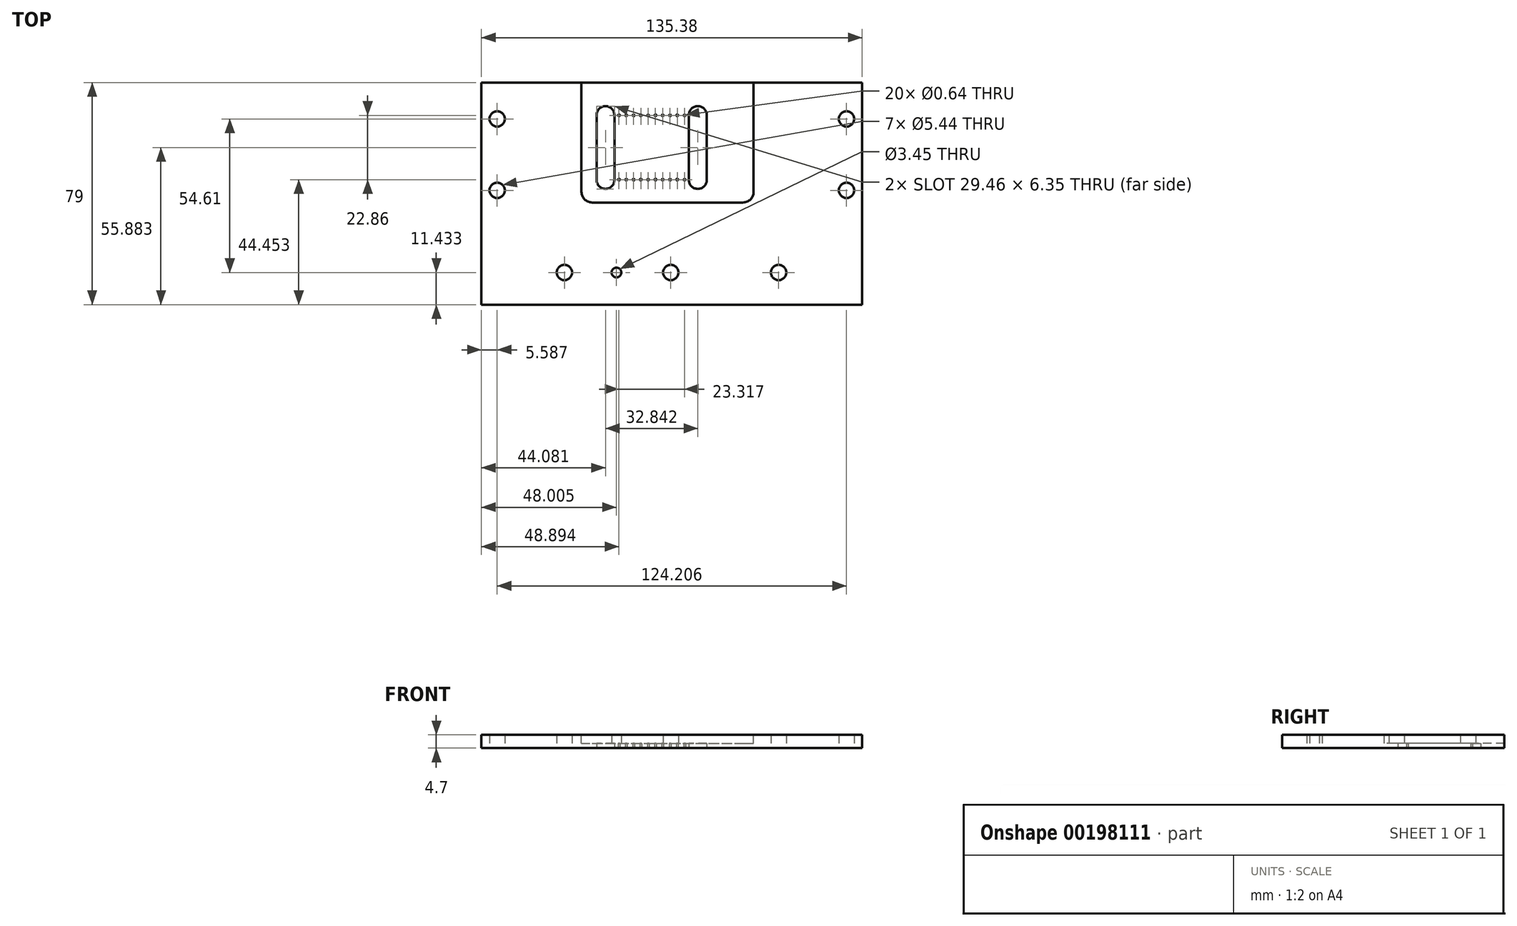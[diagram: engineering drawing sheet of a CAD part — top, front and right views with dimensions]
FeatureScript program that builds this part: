
annotation { "Feature Type Name" : "Feature", "Feature Type Description" : "" }
export const myFeature = defineFeature(function(context is Context, id is Id, definition is map)
    precondition{}
    {
        {
            var Q0;
            Q0=qCreatedBy(makeId("Top.planeOp"),FACE);
            var sketch = newSketch(context, id + "F0", { "sketchPlane" : qUnion([Q0])});
            skLineSegment(sketch, "E0.bottom", {"start": v(-67.7, 39.5) * mm, "end": v(67.7, 39.5) * mm});
            skLineSegment(sketch, "E0.top", {"start": v(-67.7, -39.5) * mm, "end": v(67.7, -39.5) * mm});
            skLineSegment(sketch, "E0.left", {"start": v(-67.7, 39.5) * mm, "end": v(-67.7, -39.5) * mm});
            skLineSegment(sketch, "E0.right", {"start": v(67.7, 39.5) * mm, "end": v(67.7, -39.5) * mm});
            skPoint(sketch, "E0.middle", {"position": v(0, 0) * mm});
            skCircle(sketch, "E1", {"center": v(-62.1, 26.54) * mm, "radius": 2.72 * mm});
            skCircle(sketch, "E2", {"center": v(62.1, 26.54) * mm, "radius": 2.72 * mm});
            skCircle(sketch, "E3", {"center": v(-62.1, 1.14) * mm, "radius": 2.72 * mm});
            skCircle(sketch, "E4", {"center": v(62.1, 1.14) * mm, "radius": 2.72 * mm});
            skCircle(sketch, "E5", {"center": v(37.95, -28.07) * mm, "radius": 2.72 * mm});
            skCircle(sketch, "E6", {"center": v(-38.2, -28.07) * mm, "radius": 2.72 * mm});
            skCircle(sketch, "E7", {"center": v(-18.8, 27.81) * mm, "radius": 0.32 * mm});
            skCircle(sketch, "E8.1.0.0", {"center": v(-16.2, 27.81) * mm, "radius": 0.32 * mm});
            skCircle(sketch, "E8.2.0.0", {"center": v(-13.61, 27.81) * mm, "radius": 0.32 * mm});
            skCircle(sketch, "E8.3.0.0", {"center": v(-11.02, 27.81) * mm, "radius": 0.32 * mm});
            skCircle(sketch, "E8.4.0.0", {"center": v(-8.43, 27.81) * mm, "radius": 0.32 * mm});
            skCircle(sketch, "E8.5.0.0", {"center": v(-5.84, 27.81) * mm, "radius": 0.32 * mm});
            skCircle(sketch, "E8.6.0.0", {"center": v(-3.25, 27.81) * mm, "radius": 0.32 * mm});
            skCircle(sketch, "E8.7.0.0", {"center": v(-0.66, 27.81) * mm, "radius": 0.32 * mm});
            skCircle(sketch, "E8.8.0.0", {"center": v(1.93, 27.81) * mm, "radius": 0.32 * mm});
            skCircle(sketch, "E8.9.0.0", {"center": v(4.52, 27.81) * mm, "radius": 0.32 * mm});
            skLineSegment(sketch, "E8.direction1", {"start": v(-18.8, 27.81) * mm, "end": v(-16.2, 27.81) * mm, "construction": true});
            skCircle(sketch, "E9", {"center": v(-18.8, 4.95) * mm, "radius": 0.32 * mm});
            skCircle(sketch, "E10.1.0.0", {"center": v(-16.2, 4.95) * mm, "radius": 0.32 * mm});
            skCircle(sketch, "E10.2.0.0", {"center": v(-13.61, 4.95) * mm, "radius": 0.32 * mm});
            skCircle(sketch, "E10.3.0.0", {"center": v(-11.02, 4.95) * mm, "radius": 0.32 * mm});
            skCircle(sketch, "E10.4.0.0", {"center": v(-8.43, 4.95) * mm, "radius": 0.32 * mm});
            skCircle(sketch, "E10.5.0.0", {"center": v(-5.84, 4.95) * mm, "radius": 0.32 * mm});
            skCircle(sketch, "E10.6.0.0", {"center": v(-3.25, 4.95) * mm, "radius": 0.32 * mm});
            skCircle(sketch, "E10.7.0.0", {"center": v(-0.66, 4.95) * mm, "radius": 0.32 * mm});
            skCircle(sketch, "E10.8.0.0", {"center": v(1.93, 4.95) * mm, "radius": 0.32 * mm});
            skCircle(sketch, "E10.9.0.0", {"center": v(4.52, 4.95) * mm, "radius": 0.32 * mm});
            skLineSegment(sketch, "E10.direction1", {"start": v(-18.8, 4.95) * mm, "end": v(-16.2, 4.95) * mm, "construction": true});
            skLineSegment(sketch, "E11.bottom", {"start": v(9.23, 31.12) * mm, "end": v(9.23, 31.12) * mm});
            skLineSegment(sketch, "E11.top", {"start": v(9.23, 1.65) * mm, "end": v(9.23, 1.65) * mm});
            skLineSegment(sketch, "E11.left", {"start": v(6.06, 27.94) * mm, "end": v(6.06, 4.83) * mm});
            skLineSegment(sketch, "E11.right", {"start": v(12.4, 27.94) * mm, "end": v(12.4, 4.83) * mm});
            skLineSegment(sketch, "E12.bottom", {"start": v(-23.6, 31.12) * mm, "end": v(-23.6, 31.12) * mm});
            skLineSegment(sketch, "E12.top", {"start": v(-23.6, 1.65) * mm, "end": v(-23.6, 1.65) * mm});
            skLineSegment(sketch, "E12.left", {"start": v(-20.43, 27.94) * mm, "end": v(-20.43, 4.83) * mm});
            skLineSegment(sketch, "E12.right", {"start": v(-26.78, 27.94) * mm, "end": v(-26.78, 4.83) * mm});
            skPoint(sketch, "E13.visualSharp", {"position": v(6.06, 31.12) * mm});
            skArc(sketch, "E13.filletArc", {"start": v(9.23, 31.12) * mm, "mid": v(6.99, 30.19) * mm, "end": v(6.06, 27.94) * mm});
            skPoint(sketch, "E14.visualSharp", {"position": v(12.4, 31.12) * mm});
            skArc(sketch, "E14.filletArc", {"start": v(12.4, 27.94) * mm, "mid": v(11.48, 30.19) * mm, "end": v(9.23, 31.12) * mm});
            skPoint(sketch, "E15.visualSharp", {"position": v(12.4, 1.65) * mm});
            skArc(sketch, "E15.filletArc", {"start": v(9.23, 1.65) * mm, "mid": v(11.48, 2.58) * mm, "end": v(12.4, 4.83) * mm});
            skPoint(sketch, "E16.visualSharp", {"position": v(6.06, 1.65) * mm});
            skArc(sketch, "E16.filletArc", {"start": v(6.06, 4.83) * mm, "mid": v(6.99, 2.58) * mm, "end": v(9.23, 1.65) * mm});
            skPoint(sketch, "E17.visualSharp", {"position": v(-20.43, 31.12) * mm});
            skArc(sketch, "E17.filletArc", {"start": v(-20.43, 27.94) * mm, "mid": v(-21.36, 30.19) * mm, "end": v(-23.6, 31.12) * mm});
            skPoint(sketch, "E18.visualSharp", {"position": v(-26.78, 31.12) * mm});
            skArc(sketch, "E18.filletArc", {"start": v(-23.6, 31.12) * mm, "mid": v(-25.85, 30.19) * mm, "end": v(-26.78, 27.94) * mm});
            skPoint(sketch, "E19.visualSharp", {"position": v(-26.78, 1.65) * mm});
            skArc(sketch, "E19.filletArc", {"start": v(-26.78, 4.83) * mm, "mid": v(-25.85, 2.58) * mm, "end": v(-23.6, 1.65) * mm});
            skPoint(sketch, "E20.visualSharp", {"position": v(-20.43, 1.65) * mm});
            skArc(sketch, "E20.filletArc", {"start": v(-23.6, 1.65) * mm, "mid": v(-21.36, 2.58) * mm, "end": v(-20.43, 4.83) * mm});
            skCircle(sketch, "E21", {"center": v(-0.38, -28.07) * mm, "radius": 2.72 * mm});
            skCircle(sketch, "E22", {"center": v(-19.69, -28.07) * mm, "radius": 1.73 * mm});
            skSolve(sketch);
        }
        {
            var Q0;
            Q0 = qSketchRegion(id + "F0", true);
            extrude(context, id + "F1", {"entities" : qUnion([Q0]), "depth" : 4.7 * mm});
        }
        {
            var Q0;
            Q0=makeQuery(id+"F1.opExtrude","CAP_FACE",FACE,{"disambiguationData":[OSD([sQuery(id+"F0.wireOp",EDGE,"E0.bottom"),sQuery(id+"F0.wireOp",EDGE,"E0.top"),sQuery(id+"F0.wireOp",EDGE,"E0.left"),sQuery(id+"F0.wireOp",EDGE,"E0.right"),sQuery(id+"F0.wireOp",EDGE,"E1"),sQuery(id+"F0.wireOp",EDGE,"E2"),sQuery(id+"F0.wireOp",EDGE,"E3"),sQuery(id+"F0.wireOp",EDGE,"E4"),sQuery(id+"F0.wireOp",EDGE,"E5"),sQuery(id+"F0.wireOp",EDGE,"E6"),sQuery(id+"F0.wireOp",EDGE,"E7"),sQuery(id+"F0.wireOp",EDGE,"E8.1.0.0"),sQuery(id+"F0.wireOp",EDGE,"E8.2.0.0"),sQuery(id+"F0.wireOp",EDGE,"E8.3.0.0"),sQuery(id+"F0.wireOp",EDGE,"E8.4.0.0"),sQuery(id+"F0.wireOp",EDGE,"E8.5.0.0"),sQuery(id+"F0.wireOp",EDGE,"E8.6.0.0"),sQuery(id+"F0.wireOp",EDGE,"E8.7.0.0"),sQuery(id+"F0.wireOp",EDGE,"E8.8.0.0"),sQuery(id+"F0.wireOp",EDGE,"E8.9.0.0"),sQuery(id+"F0.wireOp",EDGE,"E9"),sQuery(id+"F0.wireOp",EDGE,"E10.1.0.0"),sQuery(id+"F0.wireOp",EDGE,"E10.2.0.0"),sQuery(id+"F0.wireOp",EDGE,"E10.3.0.0"),sQuery(id+"F0.wireOp",EDGE,"E10.4.0.0"),sQuery(id+"F0.wireOp",EDGE,"E10.5.0.0"),sQuery(id+"F0.wireOp",EDGE,"E10.6.0.0"),sQuery(id+"F0.wireOp",EDGE,"E10.7.0.0"),sQuery(id+"F0.wireOp",EDGE,"E10.8.0.0"),sQuery(id+"F0.wireOp",EDGE,"E10.9.0.0"),sQuery(id+"F0.wireOp",EDGE,"E11.left"),sQuery(id+"F0.wireOp",EDGE,"E11.right"),sQuery(id+"F0.wireOp",EDGE,"E12.left"),sQuery(id+"F0.wireOp",EDGE,"E12.right"),sQuery(id+"F0.wireOp",EDGE,"E13.filletArc"),sQuery(id+"F0.wireOp",EDGE,"E14.filletArc"),sQuery(id+"F0.wireOp",EDGE,"E15.filletArc"),sQuery(id+"F0.wireOp",EDGE,"E16.filletArc"),sQuery(id+"F0.wireOp",EDGE,"E17.filletArc"),sQuery(id+"F0.wireOp",EDGE,"E18.filletArc"),sQuery(id+"F0.wireOp",EDGE,"E19.filletArc"),sQuery(id+"F0.wireOp",EDGE,"E20.filletArc"),sQuery(id+"F0.wireOp",EDGE,"E21"),sQuery(id+"F0.wireOp",EDGE,"E22")])],"isStart":false});
            var sketch = newSketch(context, id + "F2", { "sketchPlane" : qUnion([Q0])});
            skLineSegment(sketch, "E23.bottom", {"start": v(-32.13, 39.5) * mm, "end": v(29.08, 39.5) * mm});
            skLineSegment(sketch, "E23.top", {"start": v(-28.32, -3.18) * mm, "end": v(25.27, -3.18) * mm});
            skLineSegment(sketch, "E23.left", {"start": v(-32.13, 39.5) * mm, "end": v(-32.13, 0.63) * mm});
            skLineSegment(sketch, "E23.right", {"start": v(29.08, 39.5) * mm, "end": v(29.08, 0.63) * mm});
            skPoint(sketch, "E24.visualSharp", {"position": v(-32.13, -3.18) * mm});
            skArc(sketch, "E24.filletArc", {"start": v(-32.13, 0.63) * mm, "mid": v(-31.02, -2.06) * mm, "end": v(-28.32, -3.18) * mm});
            skPoint(sketch, "E25.visualSharp", {"position": v(29.08, -3.18) * mm});
            skArc(sketch, "E25.filletArc", {"start": v(25.27, -3.18) * mm, "mid": v(27.97, -2.06) * mm, "end": v(29.08, 0.63) * mm});
            skSolve(sketch);
        }
        {
            var Q0;
            Q0 = qSketchRegion(id + "F2", true);
            extrude(context, id + "F3", {"entities" : qUnion([Q0]), "operationType" : NewBodyOperationType.REMOVE, "oppositeDirection" : true, "depth" : 3.02 * mm});
        }
    });
